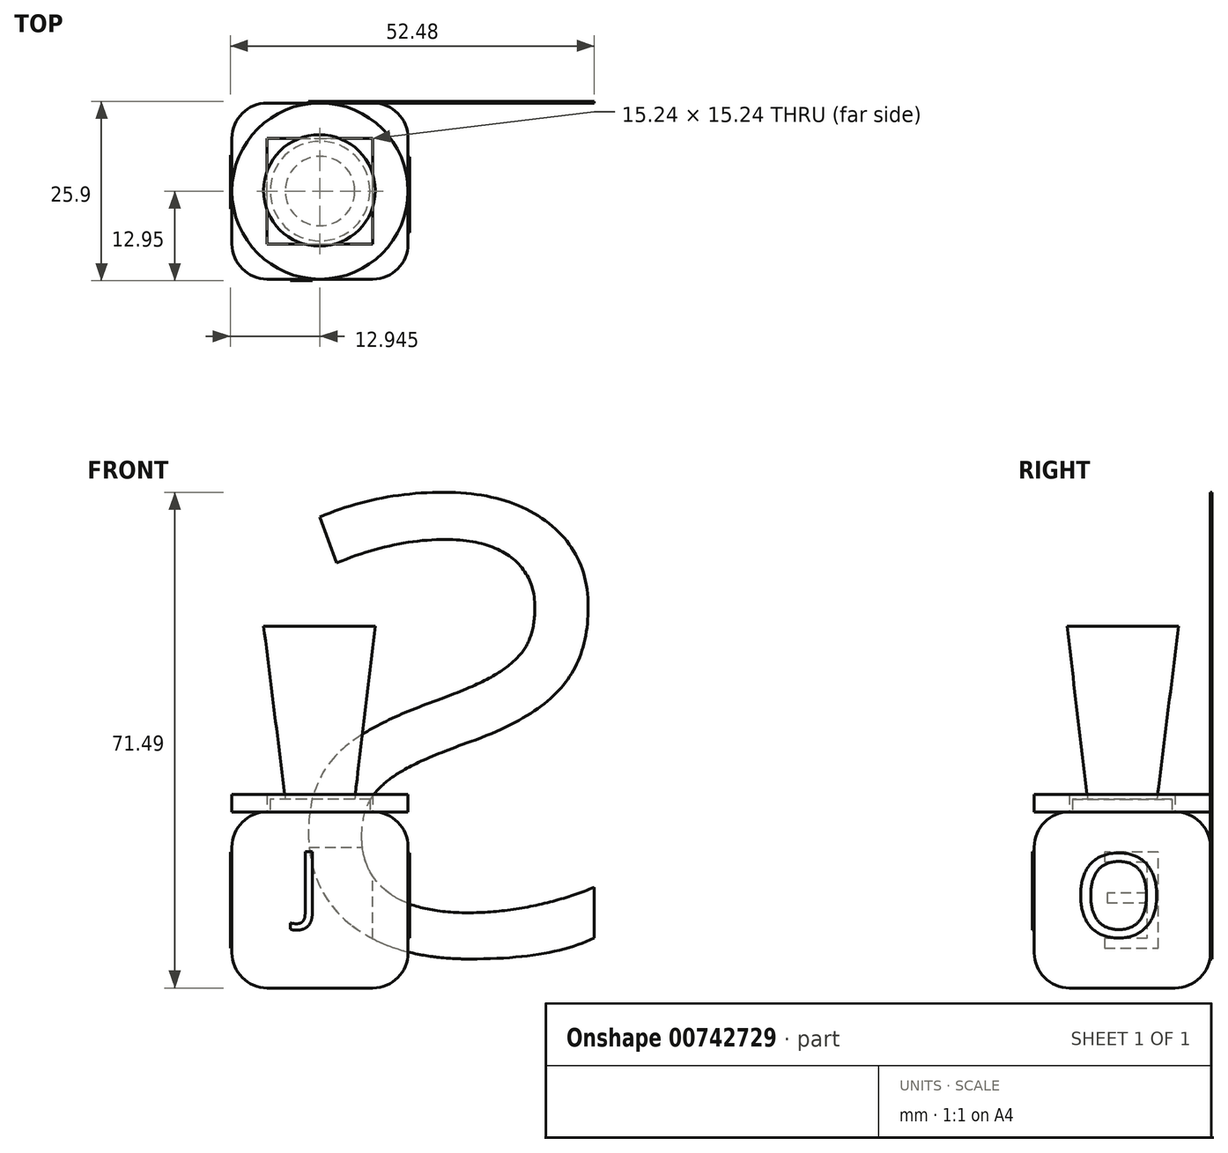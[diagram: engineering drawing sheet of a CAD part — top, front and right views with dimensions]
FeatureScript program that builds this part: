
annotation { "Feature Type Name" : "Feature", "Feature Type Description" : "" }
export const myFeature = defineFeature(function(context is Context, id is Id, definition is map)
    precondition{}
    {
        {
            var Q0;
            Q0=qCreatedBy(makeId("Front.planeOp"),FACE);
            var sketch = newSketch(context, id + "F0", { "sketchPlane" : qUnion([Q0])});
            skLineSegment(sketch, "E0", {"start": v(-45.04, 0) * mm, "end": v(-19.64, 0) * mm});
            skLineSegment(sketch, "E1", {"start": v(-45.04, 0) * mm, "end": v(-45.04, 25.4) * mm});
            skLineSegment(sketch, "E2", {"start": v(-19.64, 0) * mm, "end": v(-19.64, 25.4) * mm});
            skLineSegment(sketch, "E3", {"start": v(-45.04, 25.4) * mm, "end": v(-19.64, 25.4) * mm});
            skSolve(sketch);
        }
        {
            var Q0;
            Q0=makeQuery(id+"F0.imprint","IMPRINT",FACE,{"disambiguationData":[TD([[makeQuery(id+"F0.imprint","IMPRINT",EDGE,{"derivedFrom":sQuery(id+"F0.wireOp",EDGE,"E0")}),1.0]])]});
            extrude(context, id + "F1", {"entities" : qUnion([Q0]), "depth" : 25.4 * mm, "offsetDistance" : 25.4 * mm});
        }
        {
            var Q0;
            Q0=makeQuery(id+"F1.opExtrude","CAP_EDGE",EDGE,{"disambiguationData":[OSD([sQuery(id+"F0.wireOp",EDGE,"E3")])],"isStart":false});
            var Q1;
            Q1=makeQuery(id+"F1.opExtrude","SWEPT_EDGE",EDGE,{"disambiguationData":[OSD([sQuery(id+"F0.wireOp",EDGE,"E2"),sQuery(id+"F0.wireOp",EDGE,"E3")])]});
            var Q2;
            Q2=makeQuery(id+"F1.opExtrude","CAP_EDGE",EDGE,{"disambiguationData":[OSD([sQuery(id+"F0.wireOp",EDGE,"E2")])],"isStart":false});
            var Q3;
            Q3=makeQuery(id+"F1.opExtrude","SWEPT_EDGE",EDGE,{"disambiguationData":[OSD([sQuery(id+"F0.wireOp",EDGE,"E1"),sQuery(id+"F0.wireOp",EDGE,"E3")])]});
            var Q4;
            Q4=makeQuery(id+"F1.opExtrude","SWEPT_FACE",FACE,{"disambiguationData":[OSD([sQuery(id+"F0.wireOp",EDGE,"E3")])]});
            var Q5;
            Q5=makeQuery(id+"F1.opExtrude","CAP_FACE",FACE,{"disambiguationData":[OSD([sQuery(id+"F0.wireOp",EDGE,"E0"),sQuery(id+"F0.wireOp",EDGE,"E1"),sQuery(id+"F0.wireOp",EDGE,"E2"),sQuery(id+"F0.wireOp",EDGE,"E3")])],"isStart":false});
            var Q6;
            Q6=makeQuery(id+"F1.opExtrude","SWEPT_EDGE",EDGE,{"disambiguationData":[OSD([sQuery(id+"F0.wireOp",EDGE,"E0"),sQuery(id+"F0.wireOp",EDGE,"E2")])]});
            var Q7;
            Q7=makeQuery(id+"F1.opExtrude","SWEPT_EDGE",EDGE,{"disambiguationData":[OSD([sQuery(id+"F0.wireOp",EDGE,"E0"),sQuery(id+"F0.wireOp",EDGE,"E1")])]});
            var Q8;
            Q8=makeQuery(id+"F1.opExtrude","SWEPT_FACE",FACE,{"disambiguationData":[OSD([sQuery(id+"F0.wireOp",EDGE,"E0")])]});
            var Q9;
            Q9=makeQuery(id+"F1.opExtrude","CAP_EDGE",EDGE,{"disambiguationData":[OSD([sQuery(id+"F0.wireOp",EDGE,"E2")])],"isStart":true});
            var Q10;
            Q10=makeQuery(id+"F1.opExtrude","CAP_EDGE",EDGE,{"disambiguationData":[OSD([sQuery(id+"F0.wireOp",EDGE,"E1")])],"isStart":true});
            fillet(context, id + "F2", {"entities" : qUnion([Q0, Q1, Q2, Q3, Q4, Q5, Q6, Q7, Q8, Q9, Q10]), "radius" : 5.08 * mm, "tangentPropagation" : true, "allowEdgeOverflow" : false});
        }
        {
            var Q0;
            Q0=makeQuery(id+"F1.opExtrude","SWEPT_FACE",FACE,{"disambiguationData":[OSD([sQuery(id+"F0.wireOp",EDGE,"E3")])]});
            var sketch = newSketch(context, id + "F3", { "sketchPlane" : qUnion([Q0])});
            skCircle(sketch, "E4", {"center": v(-32.34, -12.7) * mm, "radius": 12.7 * mm});
            skPoint(sketch, "E4.centerSnap0", {"position": v(-24.72, -12.7) * mm});
            skPoint(sketch, "E4.centerSnap1", {"position": v(-32.34, -20.32) * mm});
            skSolve(sketch);
        }
        {
            var Q0;
            Q0=makeQuery(id+"F3.imprint","IMPRINT",FACE,{"disambiguationData":[TD([[makeQuery(id+"F3.imprint","IMPRINT",EDGE,{"derivedFrom":sQuery(id+"F3.wireOp",EDGE,"E4")}),1.0]])]});
            extrude(context, id + "F4", {"entities" : qUnion([Q0]), "operationType" : NewBodyOperationType.ADD, "depth" : 2.54 * mm, "offsetDistance" : 25.4 * mm});
        }
        {
            var Q0;
            Q0=makeQuery(id+"F1.opExtrude","CAP_FACE",FACE,{"disambiguationData":[OSD([sQuery(id+"F0.wireOp",EDGE,"E0"),sQuery(id+"F0.wireOp",EDGE,"E1"),sQuery(id+"F0.wireOp",EDGE,"E2"),sQuery(id+"F0.wireOp",EDGE,"E3")])],"isStart":true});
            var sketch = newSketch(context, id + "F5", { "sketchPlane" : qUnion([Q0])});
            skText(sketch, "E5", { "text": "S", "fontName": "OpenSans-Regular.ttf"});
            const initialGuessF5  = {"E5": [-0.01193, 0.00508, 1, 0, 0.06604]};
            skSetInitialGuess(sketch, initialGuessF5);
            skSolve(sketch);
        }
        {
            var Q0;
            Q0 = qSketchRegion(id + "F5", true);
            extrude(context, id + "F6", {"entities" : qUnion([Q0]), "operationType" : NewBodyOperationType.ADD, "depth" : .25 * mm, "offsetDistance" : 25.4 * mm});
        }
        {
            var Q0;
            Q0=makeQuery(id+"F1.opExtrude","SWEPT_FACE",FACE,{"disambiguationData":[OSD([sQuery(id+"F0.wireOp",EDGE,"E1")])]});
            var sketch = newSketch(context, id + "F7", { "sketchPlane" : qUnion([Q0])});
            skText(sketch, "E6", { "text": "E", "fontName": "OpenSans-Regular.ttf"});
            const initialGuessF7  = {"E6": [0.00561, 0.00573, 1, 0, 0.014]};
            skSetInitialGuess(sketch, initialGuessF7);
            skSolve(sketch);
        }
        {
            var Q0;
            Q0=makeQuery(id+"F7.imprint","IMPRINT",FACE,{"disambiguationData":[TD([[makeQuery(id+"F7.imprint","IMPRINT",EDGE,{"derivedFrom":sQuery(id+"F7.wireOp",EDGE,"E6.sketch_text.stroke-0")}),-1.0]])]});
            extrude(context, id + "F8", {"entities" : qUnion([Q0]), "operationType" : NewBodyOperationType.ADD, "depth" : .25 * mm, "offsetDistance" : 25 * mm});
        }
        {
            var Q0;
            Q0=makeQuery(id+"F1.opExtrude","CAP_FACE",FACE,{"disambiguationData":[OSD([sQuery(id+"F0.wireOp",EDGE,"E0"),sQuery(id+"F0.wireOp",EDGE,"E1"),sQuery(id+"F0.wireOp",EDGE,"E2"),sQuery(id+"F0.wireOp",EDGE,"E3")])],"isStart":false});
            var sketch = newSketch(context, id + "F9", { "sketchPlane" : qUnion([Q0])});
            skText(sketch, "E7", { "text": "J", "fontName": "OpenSans-Regular.ttf"});
            const initialGuessF9  = {"E7": [-0.03566, 0.01069, 1, 0, 0.00903]};
            skSetInitialGuess(sketch, initialGuessF9);
            skSolve(sketch);
        }
        {
            var Q0;
            Q0 = qSketchRegion(id + "F9", true);
            extrude(context, id + "F10", {"entities" : qUnion([Q0]), "operationType" : NewBodyOperationType.ADD, "depth" : .25 * mm, "offsetDistance" : 25 * mm});
        }
        {
            var Q0;
            Q0=makeQuery(id+"F1.opExtrude","SWEPT_FACE",FACE,{"disambiguationData":[OSD([sQuery(id+"F0.wireOp",EDGE,"E2")])]});
            var sketch = newSketch(context, id + "F11", { "sketchPlane" : qUnion([Q0])});
            skText(sketch, "E8", { "text": "O", "fontName": "OpenSans-Regular.ttf"});
            const initialGuessF11  = {"E8": [-0.01973, 0.00738, 1, 0, 0.01202]};
            skSetInitialGuess(sketch, initialGuessF11);
            skSolve(sketch);
        }
        {
            var Q0;
            Q0 = qSketchRegion(id + "F11", true);
            extrude(context, id + "F12", {"entities" : qUnion([Q0]), "operationType" : NewBodyOperationType.ADD, "depth" : .25 * mm, "offsetDistance" : 25 * mm});
        }
        {
            var Q0;
            Q0=makeQuery(id+"F1.opExtrude","SWEPT_FACE",FACE,{"disambiguationData":[OSD([sQuery(id+"F0.wireOp",EDGE,"E3")])]});
            var sketch = newSketch(context, id + "F13", { "sketchPlane" : qUnion([Q0])});
            skCircle(sketch, "E9", {"center": v(-32.34, -12.7) * mm, "radius": 7.19 * mm});
            skPoint(sketch, "E9.centerSnap0", {"position": v(-24.72, -12.7) * mm});
            skPoint(sketch, "E9.centerSnap1", {"position": v(-32.34, -5.08) * mm});
            skSolve(sketch);
        }
        {
            var Q0;
            Q0=makeQuery(id+"F13.imprint","IMPRINT",FACE,{"disambiguationData":[TD([[makeQuery(id+"F13.imprint","IMPRINT",EDGE,{"derivedFrom":sQuery(id+"F13.wireOp",EDGE,"E9")}),1.0]])]});
            extrude(context, id + "F14", {"entities" : qUnion([Q0]), "operationType" : NewBodyOperationType.ADD, "depth" : 1.8 * mm, "offsetDistance" : 25 * mm});
        }
        {
            var Q0;
            Q0=makeQuery(id+"F14.opExtrude","CAP_FACE",FACE,{"disambiguationData":[OSD([sQuery(id+"F13.wireOp",EDGE,"E9")])],"isStart":false});
            var sketch = newSketch(context, id + "F15", { "sketchPlane" : qUnion([Q0])});
            skCircle(sketch, "E10", {"center": v(-32.34, -12.7) * mm, "radius": 5 * mm});
            skSolve(sketch);
        }
        {
            var Q0;
            Q0=makeQuery(id+"F15.imprint","IMPRINT",FACE,{"disambiguationData":[TD([[makeQuery(id+"F15.imprint","IMPRINT",EDGE,{"derivedFrom":sQuery(id+"F15.wireOp",EDGE,"E10")}),1.0]])]});
            cPlane(context, id + "F16", {"entities" : qUnion([Q0]), "cplaneType" : CPlaneType.OFFSET, "offset" : 25 * mm, "width" : 150 * mm, "height" : 150 * mm});
        }
        {
            var Q0;
            Q0=qCreatedBy(id+"F16.planeOp",FACE);
            var sketch = newSketch(context, id + "F17", { "sketchPlane" : qUnion([Q0])});
            skCircle(sketch, "E11", {"center": v(-32.43, -12.62) * mm, "radius": 8.05 * mm});
            skSolve(sketch);
        }
        {
            var Q1;
            Q1=makeQuery(id+"F15.imprint","IMPRINT",FACE,{"disambiguationData":[TD([[makeQuery(id+"F15.imprint","IMPRINT",EDGE,{"derivedFrom":sQuery(id+"F15.wireOp",EDGE,"E10")}),1.0]])]});
            var Q2;
            Q2=makeQuery(id+"F17.imprint","IMPRINT",FACE,{"disambiguationData":[TD([[makeQuery(id+"F17.imprint","IMPRINT",EDGE,{"derivedFrom":sQuery(id+"F17.wireOp",EDGE,"E11")}),1.0]])]});
            loft(context, id + "F18", {"operationType" : NewBodyOperationType.ADD, "sheetProfilesArray" : [{ "sheetProfileEntities" : qUnion([Q1]) }, { "sheetProfileEntities" : qUnion([Q2]) }]});
        }
    });
